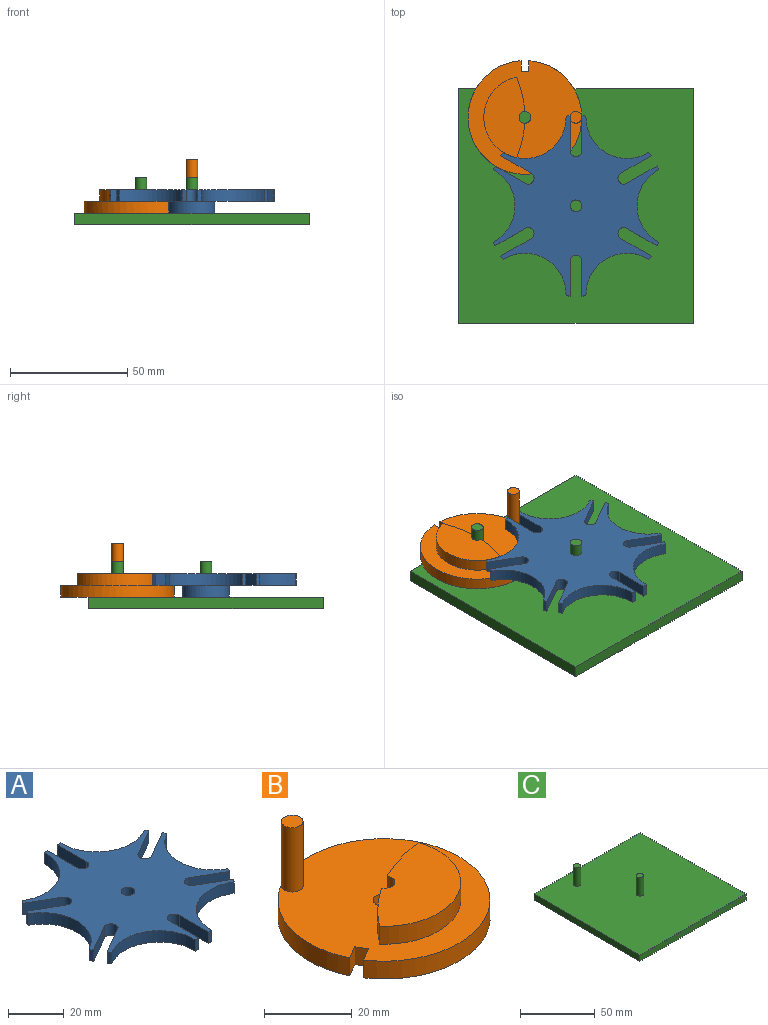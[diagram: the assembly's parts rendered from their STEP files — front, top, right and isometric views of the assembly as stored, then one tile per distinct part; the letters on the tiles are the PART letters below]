
ASSEMBLY  parts=3 mates=4
PART A: 41 faces, bbox 70.5x76.9x10 mm
  f0: plane 76.87x70.55mm, normal (0,0,-1), area 2205.8mm2, adj f1,f2,f3,f4,f5,f6,f7,f8
  f1: plane 12.92x7.46mm, normal (0.5,0.87,0), area 74.6mm2, adj f0,f2,f26,f30
  f2: cylinder r=2.5mm len=5mm, axis (0,0,-1), area 39.3mm2, adj f0,f1,f3,f26
  f3: plane 12.92x7.46mm, normal (-0.5,-0.87,0), area 74.6mm2, adj f0,f2,f26,f40
  f4: cylinder r=17.52mm len=30.93mm, axis (0,0,-1), area 189.5mm2, adj f0,f26,f39,f40
  f5: plane 12.92x7.46mm, normal (-0.5,0.87,0), area 74.6mm2, adj f0,f6,f26,f39
  f6: cylinder r=2.5mm len=5mm, axis (0,0,-1), area 39.3mm2, adj f0,f5,f7,f26
  f7: plane 12.92x7.46mm, normal (0.5,-0.87,0), area 74.6mm2, adj f0,f6,f26,f38
  f8: cylinder r=17.52mm len=26.8mm, axis (0,0,-1), area 189.5mm2, adj f0,f26,f37,f38
  f9: plane 14.92x5mm, normal (-1,0,0), area 74.6mm2, adj f0,f10,f26,f37
  f10: cylinder r=2.5mm len=5mm, axis (0,0,-1), area 39.3mm2, adj f0,f9,f11,f26
  f11: plane 14.92x5mm, normal (1,0,0), area 74.6mm2, adj f0,f10,f26,f36
  f12: cylinder r=17.52mm len=26.8mm, axis (0,0,-1), area 189.5mm2, adj f0,f26,f35,f36
  f13: plane 12.92x7.46mm, normal (-0.5,-0.87,0), area 74.6mm2, adj f0,f14,f26,f35
  f14: cylinder r=2.5mm len=5mm, axis (0,0,-1), area 39.3mm2, adj f0,f13,f15,f26
  f15: plane 12.92x7.46mm, normal (0.5,0.87,0), area 74.6mm2, adj f0,f14,f26,f34
  f16: cylinder r=17.52mm len=30.93mm, axis (0,0,-1), area 189.5mm2, adj f0,f26,f33,f34
  f17: plane 12.92x7.46mm, normal (0.5,-0.87,0), area 74.6mm2, adj f0,f18,f26,f33
  f18: cylinder r=2.5mm len=5mm, axis (0,0,-1), area 39.3mm2, adj f0,f17,f19,f26
  f19: plane 12.92x7.46mm, normal (-0.5,0.87,0), area 74.6mm2, adj f0,f18,f26,f32
  f20: cylinder r=17.52mm len=26.8mm, axis (0,0,-1), area 189.5mm2, adj f0,f26,f31,f32
  f21: plane 14.92x5mm, normal (1,0,0), area 74.6mm2, adj f0,f22,f26,f31
  f22: cylinder r=2.5mm len=5mm, axis (0,0,-1), area 39.3mm2, adj f0,f21,f23,f26
  f23: plane 14.92x5mm, normal (-1,0,0), area 74.6mm2, adj f0,f22,f26,f29
  f24: cylinder r=17.52mm len=26.8mm, axis (0,0,-1), area 189.5mm2, adj f0,f26,f29,f30
  f25: cylinder r=2.5mm len=10mm, axis (0,0,-1), area 157.1mm2, adj f26,f27
  f26: plane 76.87x70.55mm, normal (0,0,1), area 2500.3mm2, adj f1,f2,f3,f4,f5,f6,f7,f8
  f27: plane 20x20mm, normal (0,0,-1), area 294.5mm2, adj f25,f28
  f28: cylinder r=10mm len=20mm, axis (0,0,-1), area 314.2mm2, adj f0,f27
  f29: cylinder r=38.51mm len=5mm, axis (0,0,-1), area 8.7mm2, adj f0,f23,f24,f26
  f30: cylinder r=38.51mm len=5mm, axis (0,0,-1), area 8.7mm2, adj f0,f1,f24,f26
  f31: cylinder r=38.51mm len=5mm, axis (0,0,-1), area 8.7mm2, adj f0,f20,f21,f26
  f32: cylinder r=38.51mm len=5mm, axis (0,0,-1), area 8.7mm2, adj f0,f19,f20,f26
  f33: cylinder r=38.51mm len=5mm, axis (0,0,-1), area 8.7mm2, adj f0,f16,f17,f26
  f34: cylinder r=38.51mm len=5mm, axis (0,0,-1), area 8.7mm2, adj f0,f15,f16,f26
  f35: cylinder r=38.51mm len=5mm, axis (0,0,-1), area 8.7mm2, adj f0,f12,f13,f26
  f36: cylinder r=38.51mm len=5mm, axis (0,0,-1), area 8.7mm2, adj f0,f11,f12,f26
  f37: cylinder r=38.51mm len=5mm, axis (0,0,-1), area 8.7mm2, adj f0,f8,f9,f26
  f38: cylinder r=38.51mm len=5mm, axis (0,0,-1), area 8.7mm2, adj f0,f7,f8,f26
  f39: cylinder r=38.51mm len=5mm, axis (0,0,-1), area 8.7mm2, adj f0,f4,f5,f26
  f40: cylinder r=38.51mm len=5mm, axis (0,0,-1), area 8.7mm2, adj f0,f3,f4,f26
PART B: 13 faces, bbox 48.5x48.5x23 mm
  f0: plane 48.45x48.45mm, normal (0,0,1), area 1357.9mm2, adj f2,f3,f4,f5,f6,f8,f10,f11
  f1: plane 48.45x48.45mm, normal (0,0,-1), area 1808.8mm2, adj f2,f3,f10,f11,f12
  f2: cylinder r=24.22mm len=48.45mm, axis (0,0,-1), area 744.5mm2, adj f0,f1,f10,f12
  f3: cylinder r=2.5mm len=10mm, axis (0,0,-1), area 117.1mm2, adj f0,f1,f4,f6,f7
  f4: cylinder r=43.51mm len=10.97mm, axis (0,0,-1), area 75.7mm2, adj f0,f3,f5,f7
  f5: cylinder r=17.52mm len=30.63mm, axis (0,0,-1), area 239.7mm2, adj f0,f4,f6,f7
  f6: cylinder r=43.51mm len=14.43mm, axis (0,0,-1), area 75.7mm2, adj f0,f3,f5,f7
  f7: plane 30.63x23.05mm, normal (0,0,1), area 431.3mm2, adj f3,f4,f5,f6
  f8: cylinder r=2.5mm len=18mm, axis (0,0,-1), area 282.7mm2, adj f0,f9
  f9: plane 5x5mm, normal (0,0,1), area 19.6mm2, adj f8
  f10: plane 5x3.95mm, normal (-0.5,0.87,0), area 22.8mm2, adj f0,f1,f2,f11
  f11: plane 5x2.86mm, normal (-0.87,-0.5,0), area 16.5mm2, adj f0,f1,f10,f12
  f12: plane 5x3.95mm, normal (0.5,-0.87,0), area 22.8mm2, adj f0,f1,f2,f11
PART C: 10 faces, bbox 100x100x20 mm
  f0: plane 100x5mm, normal (1,0,0), area 500mm2, adj f1,f3,f4,f5
  f1: plane 100x5mm, normal (0,1,0), area 500mm2, adj f0,f2,f4,f5
  f2: plane 100x5mm, normal (-1,0,0), area 500mm2, adj f1,f3,f4,f5
  f3: plane 100x5mm, normal (0,-1,0), area 500mm2, adj f0,f2,f4,f5
  f4: plane 100x100mm, normal (0,0,-1), area 10000mm2, adj f0,f1,f2,f3
  f5: plane 100x100mm, normal (0,0,1), area 9960.7mm2, adj f0,f1,f2,f3,f6,f8
  f6: cylinder r=2.5mm len=15mm, axis (0,0,-1), area 235.6mm2, adj f5,f7
  f7: plane 5x5mm, normal (0,0,1), area 19.6mm2, adj f6
  f8: cylinder r=2.5mm len=15mm, axis (0,0,-1), area 235.6mm2, adj f5,f9
  f9: plane 5x5mm, normal (0,0,1), area 19.6mm2, adj f8
PLACE A rot(axis=(0,0,1),60deg) t=(0,0,0)mm
PLACE B rot(axis=(0,0,-1),120deg) t=(-65.27,37.68,0)mm
PLACE C at identity fixed
MATE revolute B.f2 <-> C.f6  axis (0,0,-1) through (-21.76,37.68,0)mm
MATE revolute C.f8 <-> A.f25  axis (0,0,1) through (0,0,0)mm
MATE parallel B.f10 <-> C.f0  axis (1,0,0) through (-23.41,59.57,2.5)mm
MATE parallel A.f7 <-> C.f0  axis (1,0,0) through (-2.5,30.97,7.5)mm
